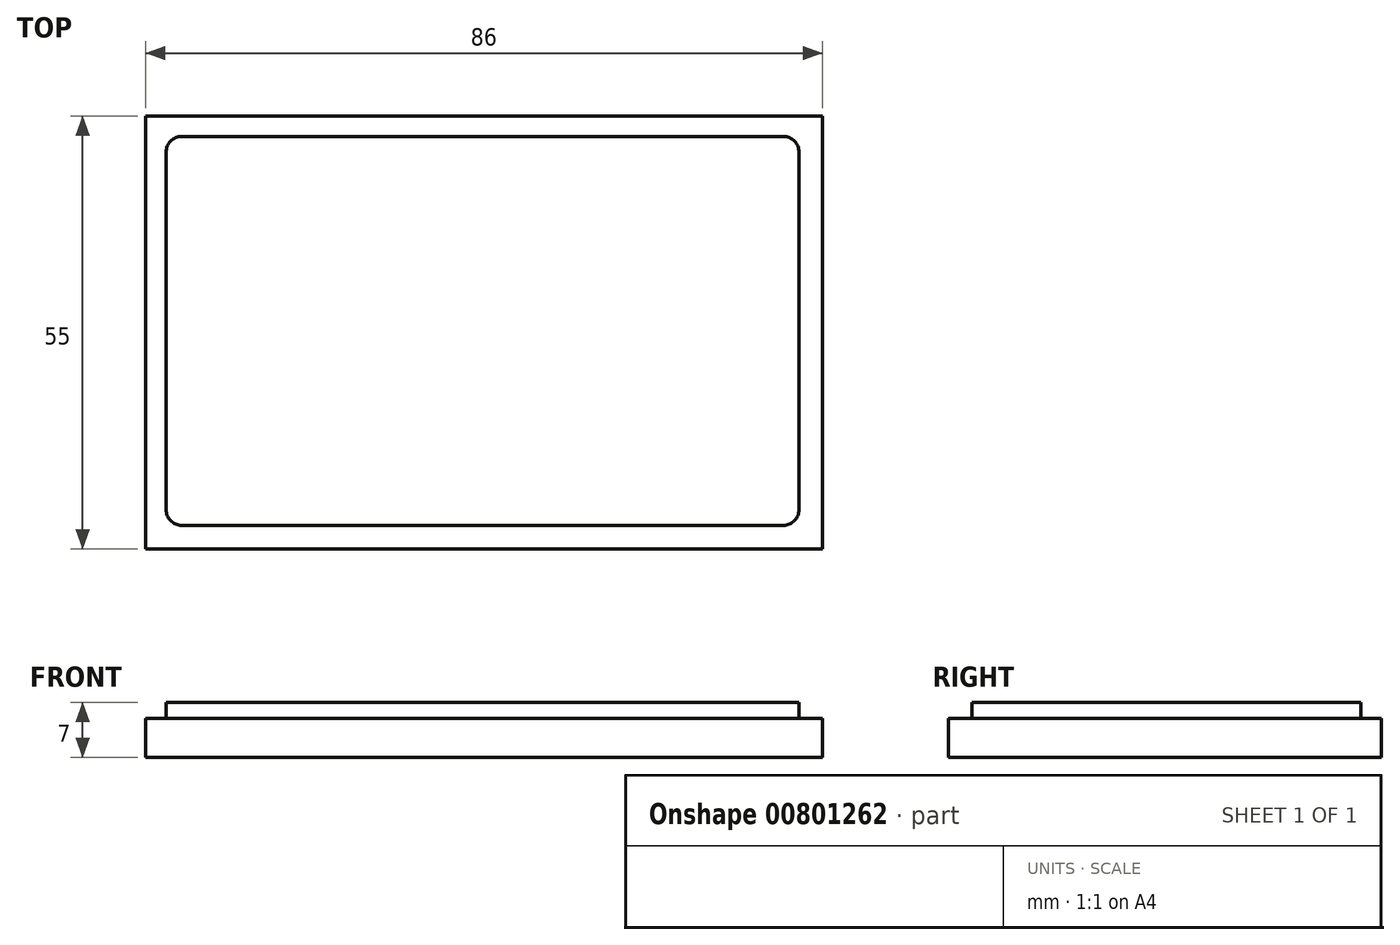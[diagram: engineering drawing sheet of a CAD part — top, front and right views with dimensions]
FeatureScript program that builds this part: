
annotation { "Feature Type Name" : "Feature", "Feature Type Description" : "" }
export const myFeature = defineFeature(function(context is Context, id is Id, definition is map)
    precondition{}
    {
        {
            var Q0;
            Q0=qCreatedBy(makeId("Top.planeOp"),FACE);
            var sketch = newSketch(context, id + "F0", { "sketchPlane" : qUnion([Q0])});
            skLineSegment(sketch, "E0", {"start": v(-43, 27.5) * mm, "end": v(43, 27.5) * mm});
            skLineSegment(sketch, "E1", {"start": v(43, 27.5) * mm, "end": v(43, -27.5) * mm});
            skLineSegment(sketch, "E2", {"start": v(43, -27.5) * mm, "end": v(-43, -27.5) * mm});
            skLineSegment(sketch, "E3", {"start": v(-43, -27.5) * mm, "end": v(-43, 27.5) * mm});
            skPoint(sketch, "E4.endSnap0", {"position": v(-43, 0) * mm});
            skSolve(sketch);
        }
        {
            var Q0;
            Q0=makeQuery(id+"F0.imprint","IMPRINT",FACE,{"disambiguationData":[TD([[makeQuery(id+"F0.imprint","IMPRINT",EDGE,{"derivedFrom":sQuery(id+"F0.wireOp",EDGE,"E0")}),-1.0]])]});
            extrude(context, id + "F1", {"entities" : qUnion([Q0]), "depth" : 5 * mm, "offsetDistance" : 25 * mm});
        }
        {
            var Q0;
            Q0=makeQuery(id+"F1.opExtrude","CAP_FACE",FACE,{"disambiguationData":[OSD([sQuery(id+"F0.wireOp",EDGE,"E0"),sQuery(id+"F0.wireOp",EDGE,"E1"),sQuery(id+"F0.wireOp",EDGE,"E2"),sQuery(id+"F0.wireOp",EDGE,"E3")])],"isStart":false});
            var sketch = newSketch(context, id + "F2", { "sketchPlane" : qUnion([Q0])});
            skLineSegment(sketch, "E5", {"start": v(-40.4, 24.9) * mm, "end": v(40, 24.9) * mm});
            skLineSegment(sketch, "E6", {"start": v(40, 24.9) * mm, "end": v(40, -24.5) * mm});
            skLineSegment(sketch, "E7", {"start": v(40, -24.5) * mm, "end": v(-40.4, -24.5) * mm});
            skLineSegment(sketch, "E8", {"start": v(-40.4, -24.5) * mm, "end": v(-40.4, 24.9) * mm});
            skSolve(sketch);
        }
        {
            var Q0;
            Q0=makeQuery(id+"F2.imprint","IMPRINT",FACE,{"disambiguationData":[TD([[makeQuery(id+"F2.imprint","IMPRINT",EDGE,{"derivedFrom":sQuery(id+"F2.wireOp",EDGE,"E5")}),-1.0]])]});
            extrude(context, id + "F3", {"entities" : qUnion([Q0]), "operationType" : NewBodyOperationType.ADD, "depth" : 2 * mm, "offsetDistance" : 25 * mm});
        }
        {
            var Q0;
            Q0=makeQuery(id+"F3.opExtrude","SWEPT_EDGE",EDGE,{"disambiguationData":[OSD([sQuery(id+"F2.wireOp",EDGE,"E7"),sQuery(id+"F2.wireOp",EDGE,"E8")])]});
            var Q1;
            Q1=makeQuery(id+"F3.opExtrude","SWEPT_EDGE",EDGE,{"disambiguationData":[OSD([sQuery(id+"F2.wireOp",EDGE,"E5"),sQuery(id+"F2.wireOp",EDGE,"E8")])]});
            var Q2;
            Q2=makeQuery(id+"F3.opExtrude","SWEPT_EDGE",EDGE,{"disambiguationData":[OSD([sQuery(id+"F2.wireOp",EDGE,"E6"),sQuery(id+"F2.wireOp",EDGE,"E7")])]});
            var Q3;
            Q3=makeQuery(id+"F3.opExtrude","SWEPT_EDGE",EDGE,{"disambiguationData":[OSD([sQuery(id+"F2.wireOp",EDGE,"E5"),sQuery(id+"F2.wireOp",EDGE,"E6")])]});
            fillet(context, id + "F4", {"entities" : qUnion([Q0, Q1, Q2, Q3]), "radius" : 2 * mm, "tangentPropagation" : true, "allowEdgeOverflow" : false});
        }
    });
